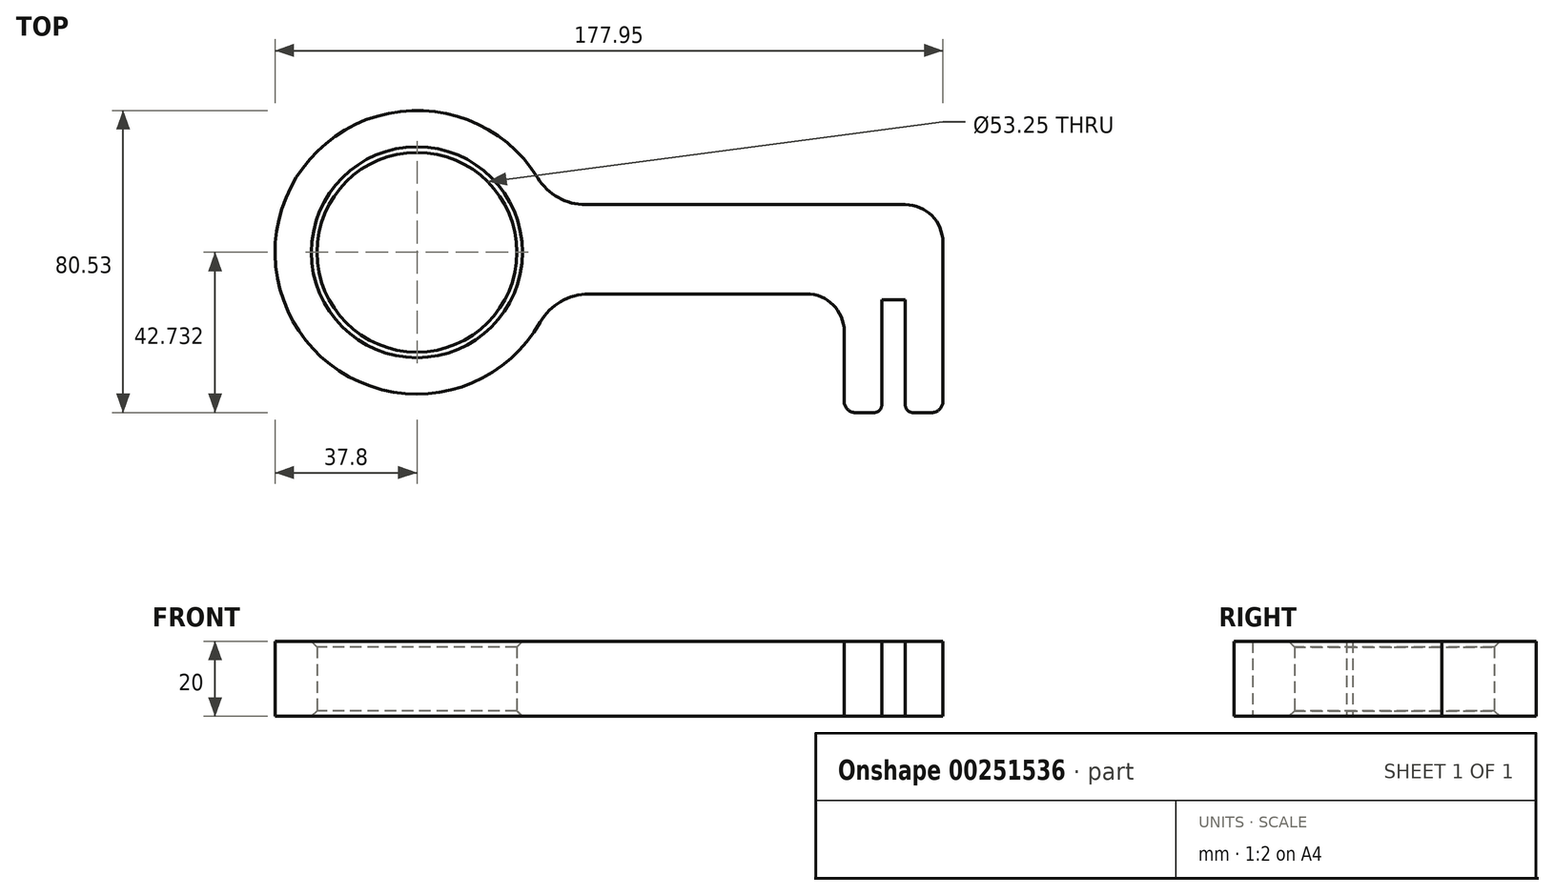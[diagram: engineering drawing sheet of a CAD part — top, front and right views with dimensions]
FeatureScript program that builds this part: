
annotation { "Feature Type Name" : "Feature", "Feature Type Description" : "" }
export const myFeature = defineFeature(function(context is Context, id is Id, definition is map)
    precondition{}
    {
        {
            var Q0;
            Q0=qCreatedBy(makeId("Top.planeOp"),FACE);
            var sketch = newSketch(context, id + "F0", { "sketchPlane" : qUnion([Q0])});
            skLineSegment(sketch, "E0", {"start": v(2, 0) * mm, "end": v(7, 0) * mm});
            skLineSegment(sketch, "E1", {"start": v(0, 30) * mm, "end": v(-6.3, 30) * mm});
            skLineSegment(sketch, "E2", {"start": v(-6.3, 30) * mm, "end": v(-6.3, 2) * mm});
            skLineSegment(sketch, "E3", {"start": v(-8.3, 0) * mm, "end": v(-13.3, 0) * mm});
            skLineSegment(sketch, "E4", {"start": v(10, 45.4) * mm, "end": v(10, 3) * mm});
            skPoint(sketch, "E5.visualSharp", {"position": v(-16.3, 0) * mm});
            skPoint(sketch, "E6.visualSharp", {"position": v(10, 0) * mm});
            skArc(sketch, "E6.filletArc", {"start": v(7, 0) * mm, "mid": v(9.12, 0.88) * mm, "end": v(10, 3) * mm});
            skPoint(sketch, "E7.visualSharp", {"position": v(-6.3, 0) * mm});
            skArc(sketch, "E7.filletArc", {"start": v(-8.3, 0) * mm, "mid": v(-6.89, 0.59) * mm, "end": v(-6.3, 2) * mm});
            skLineSegment(sketch, "E8", {"start": v(0, 30) * mm, "end": v(0, 2) * mm});
            skPoint(sketch, "E9.visualSharp", {"position": v(0, 0) * mm});
            skArc(sketch, "E9.filletArc", {"start": v(0, 2) * mm, "mid": v(0.59, 0.59) * mm, "end": v(2, 0) * mm});
            skCircle(sketch, "E10", {"center": v(-130.15, 42.73) * mm, "radius": 26.62 * mm});
            skPoint(sketch, "E11", {"position": v(-3.15, 30) * mm});
            skLineSegment(sketch, "E12", {"start": v(-85.18, 55.4) * mm, "end": v(0, 55.4) * mm});
            skPoint(sketch, "E13.visualSharp", {"position": v(10, 55.4) * mm});
            skArc(sketch, "E13.filletArc", {"start": v(10, 45.4) * mm, "mid": v(7.07, 52.47) * mm, "end": v(0, 55.4) * mm});
            skLineSegment(sketch, "E14", {"start": v(-101.55, 0) * mm, "end": v(-101.55, 142) * mm, "construction": true});
            skArc(sketch, "E15", {"start": v(-97.96, 62.54) * mm, "mid": v(-167.94, 42.08) * mm, "end": v(-97.3, 24.04) * mm});
            skLineSegment(sketch, "E16.trimOffspring", {"start": v(-84.25, 31.63) * mm, "end": v(-26.3, 31.63) * mm});
            skPoint(sketch, "E17.visualSharp", {"position": v(-94.54, 55.4) * mm});
            skArc(sketch, "E17.filletArc", {"start": v(-97.96, 62.54) * mm, "mid": v(-92.5, 57.3) * mm, "end": v(-85.18, 55.4) * mm});
            skPoint(sketch, "E18.visualSharp", {"position": v(-94.02, 31.63) * mm});
            skArc(sketch, "E18.filletArc", {"start": v(-84.25, 31.63) * mm, "mid": v(-91.8, 29.6) * mm, "end": v(-97.3, 24.04) * mm});
            skLineSegment(sketch, "E19", {"start": v(-16.3, 3) * mm, "end": v(-16.3, 21.63) * mm});
            skArc(sketch, "E20.filletArc", {"start": v(-16.3, 3) * mm, "mid": v(-15.42, 0.88) * mm, "end": v(-13.3, 0) * mm});
            skPoint(sketch, "E21.visualSharp", {"position": v(-16.3, 31.63) * mm});
            skArc(sketch, "E21.filletArc", {"start": v(-16.3, 21.63) * mm, "mid": v(-19.23, 28.7) * mm, "end": v(-26.3, 31.63) * mm});
            skSolve(sketch);
        }
        {
            var Q0;
            Q0=makeQuery(id+"F0.imprint","IMPRINT",FACE,{"disambiguationData":[TD([[makeQuery(id+"F0.imprint","IMPRINT",EDGE,{"derivedFrom":sQuery(id+"F0.wireOp",EDGE,"E0")}),1.0]])]});
            extrude(context, id + "F1", {"entities" : qUnion([Q0]), "depth" : (20) * mm});
        }
        {
            var Q0;
            Q0=makeQuery(id+"F1.opExtrude","CAP_EDGE",EDGE,{"disambiguationData":[OSD([sQuery(id+"F0.wireOp",EDGE,"E10")])],"isStart":true});
            var Q1;
            Q1=makeQuery(id+"F1.opExtrude","CAP_EDGE",EDGE,{"disambiguationData":[OSD([sQuery(id+"F0.wireOp",EDGE,"E10")])],"isStart":false});
            chamfer(context, id + "F2", {"entities" : qUnion([Q0, Q1]), "width" : 1.5 * mm, "tangentPropagation" : true});
        }
    });
